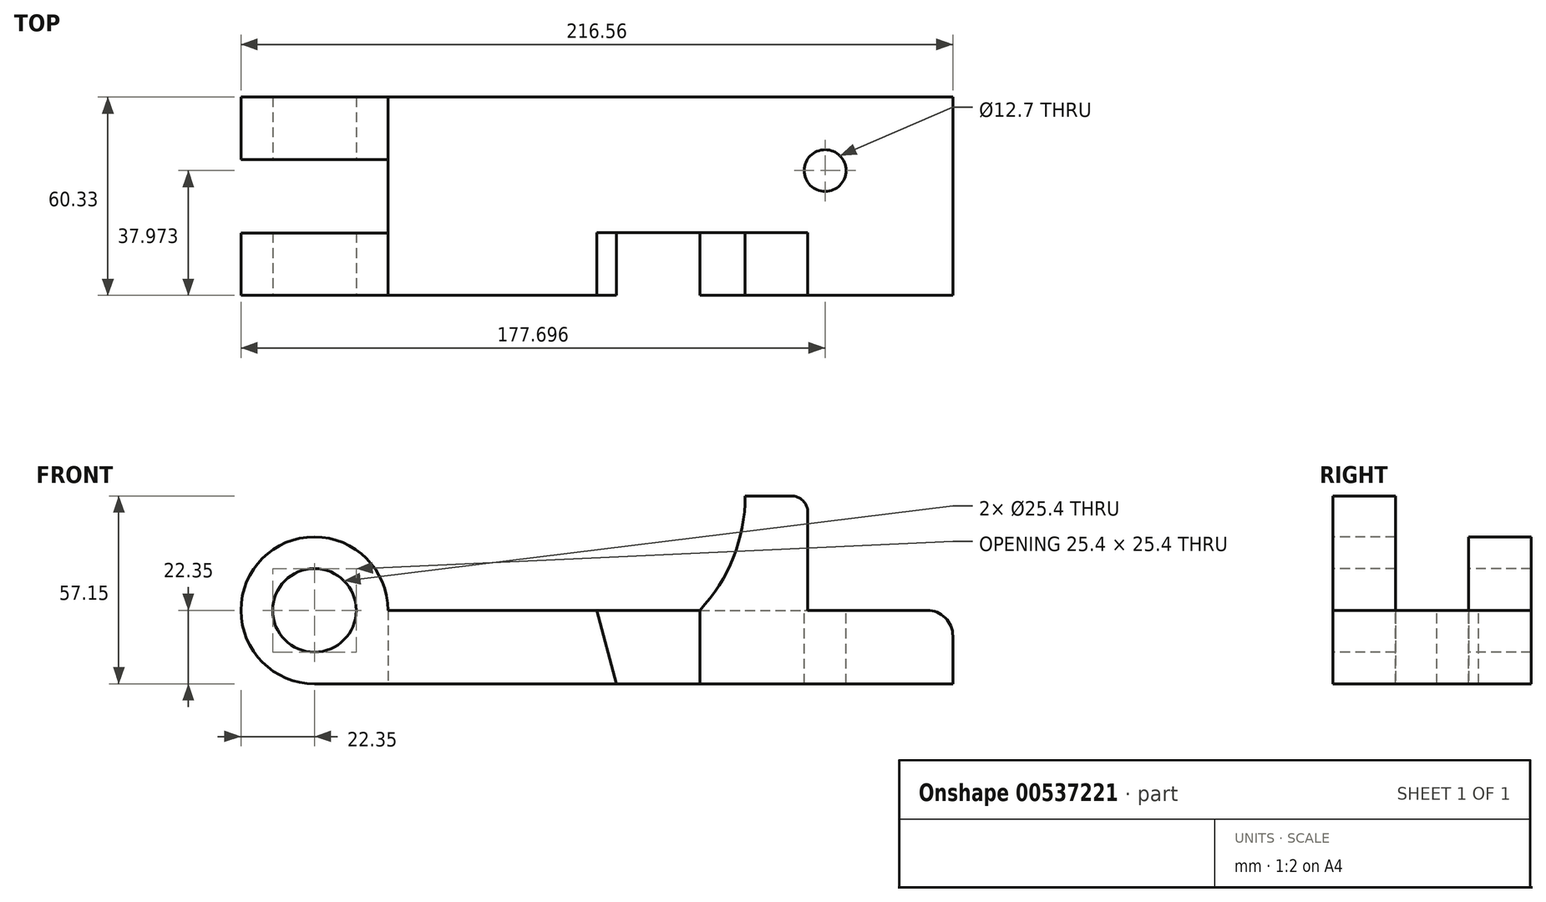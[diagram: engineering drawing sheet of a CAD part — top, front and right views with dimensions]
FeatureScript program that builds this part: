
annotation { "Feature Type Name" : "Feature", "Feature Type Description" : "" }
export const myFeature = defineFeature(function(context is Context, id is Id, definition is map)
    precondition{}
    {
        {
            var Q0;
            Q0=qCreatedBy(makeId("Front.planeOp"),FACE);
            var sketch = newSketch(context, id + "F0", { "sketchPlane" : qUnion([Q0])});
            skCircle(sketch, "E0", {"center": v(0, 0) * mm, "radius": 22.35 * mm});
            skCircle(sketch, "E1", {"center": v(0, 0) * mm, "radius": 12.7 * mm});
            skLineSegment(sketch, "E2", {"start": v(0, -22.35) * mm, "end": v(91.85, -22.35) * mm});
            skLineSegment(sketch, "E3", {"start": v(91.85, -22.35) * mm, "end": v(117.25, -22.35) * mm});
            skLineSegment(sketch, "E4", {"start": v(117.25, -22.35) * mm, "end": v(194.2, -22.35) * mm});
            skLineSegment(sketch, "E5", {"start": v(0, 62.8) * mm, "end": v(0, -59.04) * mm, "construction": true});
            skLineSegment(sketch, "E6", {"start": v(22.35, 0) * mm, "end": v(85.85, 0) * mm});
            skLineSegment(sketch, "E7", {"start": v(85.85, 0) * mm, "end": v(91.85, -22.35) * mm});
            skLineSegment(sketch, "E8", {"start": v(117.25, 0) * mm, "end": v(117.25, -22.35) * mm});
            skLineSegment(sketch, "E9", {"start": v(85.85, 0) * mm, "end": v(117.25, 0) * mm});
            skPoint(sketch, "E10", {"position": v(-22.35, 0) * mm});
            skLineSegment(sketch, "E11", {"start": v(194.2, -22.35) * mm, "end": v(194.2, -7.87) * mm});
            skPoint(sketch, "E11.endSnap0", {"position": v(54.1, 0) * mm});
            skLineSegment(sketch, "E12", {"start": v(186.33, 0) * mm, "end": v(150.09, 0) * mm});
            skLineSegment(sketch, "E13", {"start": v(150.09, 0) * mm, "end": v(150.09, 29.72) * mm});
            skLineSegment(sketch, "E14", {"start": v(145, 34.8) * mm, "end": v(131.04, 34.8) * mm});
            skArc(sketch, "E15", {"start": v(117.25, 0) * mm, "mid": v(127.46, 16.08) * mm, "end": v(131.04, 34.8) * mm});
            skPoint(sketch, "E16.visualSharp", {"position": v(150.09, 34.8) * mm});
            skArc(sketch, "E16.filletArc", {"start": v(150.09, 29.72) * mm, "mid": v(148.6, 33.31) * mm, "end": v(145, 34.8) * mm});
            skPoint(sketch, "E17.visualSharp", {"position": v(194.2, 0) * mm});
            skArc(sketch, "E17.filletArc", {"start": v(194.2, -7.87) * mm, "mid": v(191.9, -2.3) * mm, "end": v(186.33, 0) * mm});
            skLineSegment(sketch, "E18", {"start": v(117.25, 0) * mm, "end": v(150.09, 0) * mm});
            skSolve(sketch);
        }
        {
            var Q0;
            Q0=makeQuery(id+"F0.imprint","IMPRINT",FACE,{"disambiguationData":[TD([[makeQuery(id+"F0.imprint","IMPRINT",EDGE,{"derivedFrom":sQuery(id+"F0.wireOp",EDGE,"E1")}),-1.0]])]});
            extrude(context, id + "F1", {"entities" : qUnion([Q0]), "oppositeDirection" : true, "depth" : 60.32 * mm, "offsetDistance" : 25.4 * mm});
        }
        {
            var Q0;
            Q0=makeQuery(id+"F0.imprint","IMPRINT",FACE,{"disambiguationData":[TD([[makeQuery(id+"F0.imprint","IMPRINT",EDGE,{"derivedFrom":sQuery(id+"F0.wireOp",EDGE,"E4")}),1.0]])]});
            var Q1;
            {var subQ0=sQuery(id+"F0.wireOp",EDGE,"E2");Q1=makeQuery(id+"F0.imprint","IMPRINT",FACE,{"disambiguationData":[TD([[makeQuery(id+"F0.imprint","IMPRINT",EDGE,{"derivedFrom":subQ0}),1.0]])]});}
            extrude(context, id + "F2", {"entities" : qUnion([Q0, Q1]), "operationType" : NewBodyOperationType.ADD, "oppositeDirection" : true, "depth" : 60.32 * mm, "offsetDistance" : 25.4 * mm});
        }
        {
            var Q0;
            Q0=makeQuery(id+"F0.imprint","IMPRINT",FACE,{"disambiguationData":[TD([[makeQuery(id+"F0.imprint","IMPRINT",EDGE,{"derivedFrom":sQuery(id+"F0.wireOp",EDGE,"E3")}),1.0]])]});
            var Q1;
            Q1=makeQuery(id+"F2.opExtrude","CAP_VERTEX",VERTEX,{"disambiguationData":[OSD([sQuery(id+"F0.wireOp",EDGE,"E8"),sQuery(id+"F0.wireOp",EDGE,"E9"),sQuery(id+"F0.wireOp",EDGE,"E15")])],"isStart":false});
            extrude(context, id + "F3", {"entities" : qUnion([Q0]), "operationType" : NewBodyOperationType.ADD, "endBound" : BoundingType.UP_TO_VERTEX, "oppositeDirection" : true, "depth" : 97.03 * mm, "endBoundEntityVertex" : qUnion([Q1]), "offsetDistance" : 25.4 * mm});
        }
        {
            var Q0;
            Q0=makeQuery(id+"F0.imprint","IMPRINT",FACE,{"disambiguationData":[TD([[makeQuery(id+"F0.imprint","IMPRINT",EDGE,{"derivedFrom":sQuery(id+"F0.wireOp",EDGE,"E3")}),1.0]])]});
            extrude(context, id + "F4", {"entities" : qUnion([Q0]), "operationType" : NewBodyOperationType.REMOVE, "oppositeDirection" : true, "depth" : 19.05 * mm, "offsetDistance" : 25.4 * mm});
        }
        {
            var Q0;
            Q0=makeQuery(id+"F0.imprint","IMPRINT",FACE,{"disambiguationData":[TD([[makeQuery(id+"F0.imprint","IMPRINT",EDGE,{"derivedFrom":sQuery(id+"F0.wireOp",EDGE,"E13")}),1.0]])]});
            extrude(context, id + "F5", {"entities" : qUnion([Q0]), "operationType" : NewBodyOperationType.ADD, "oppositeDirection" : true, "depth" : 19.05 * mm, "offsetDistance" : 25.4 * mm});
        }
        {
            var Q0;
            Q0=qCreatedBy(makeId("Top.planeOp"),FACE);
            var sketch = newSketch(context, id + "F6", { "sketchPlane" : qUnion([Q0])});
            skLineSegment(sketch, "E19", {"start": v(22.35, 0) * mm, "end": v(22.35, 60.33) * mm});
            skLineSegment(sketch, "E20", {"start": v(-22.35, 0) * mm, "end": v(-22.35, 19) * mm, "construction": true});
            skLineSegment(sketch, "E21", {"start": v(-22.35, 60.33) * mm, "end": v(-22.35, 41.33) * mm, "construction": true});
            skLineSegment(sketch, "E22", {"start": v(-22.35, 41.33) * mm, "end": v(22.35, 41.33) * mm});
            skLineSegment(sketch, "E23", {"start": v(-22.35, 41.33) * mm, "end": v(-22.35, 19) * mm});
            skLineSegment(sketch, "E24", {"start": v(22.35, 19) * mm, "end": v(22.35, 41.33) * mm});
            skLineSegment(sketch, "E25", {"start": v(-22.35, 19) * mm, "end": v(22.35, 19) * mm});
            skSolve(sketch);
        }
        {
            var Q0;
            Q0 = qSketchRegion(id + "F6", true);
            extrude(context, id + "F7", {"entities" : qUnion([Q0]), "operationType" : NewBodyOperationType.REMOVE, "depth" : 73.66 * mm, "offsetDistance" : 25.4 * mm, "symmetric" : true});
        }
        {
            var Q0;
            Q0=makeQuery(id+"F3.boolean.opBoolean","MERGE",FACE,{"derivedFrom":[makeQuery(id+"F2.opExtrude","SWEPT_FACE",FACE,{"disambiguationData":[OSD([sQuery(id+"F0.wireOp",EDGE,"E6")])]}),makeQuery(id+"F2.opExtrude","SWEPT_FACE",FACE,{"disambiguationData":[OSD([sQuery(id+"F0.wireOp",EDGE,"E12"),sQuery(id+"F0.wireOp",EDGE,"E18")])]}),makeQuery(id+"F3.opExtrude","SWEPT_FACE",FACE,{"disambiguationData":[OSD([sQuery(id+"F0.wireOp",EDGE,"E9")])]})]});
            var sketch = newSketch(context, id + "F8", { "sketchPlane" : qUnion([Q0])});
            skLineSegment(sketch, "E26.0", {"start": v(194.2, 60.33) * mm, "end": v(186.33, 60.33) * mm});
            skLineSegment(sketch, "E27", {"start": v(194.2, 60.33) * mm, "end": v(155.35, 60.33) * mm, "construction": true});
            skLineSegment(sketch, "E28", {"start": v(155.35, 60.33) * mm, "end": v(155.35, 37.97) * mm, "construction": true});
            skCircle(sketch, "E29", {"center": v(155.35, 37.97) * mm, "radius": 6.35 * mm});
            skSolve(sketch);
        }
        {
            var Q0;
            Q0 = qSketchRegion(id + "F8", true);
            extrude(context, id + "F9", {"entities" : qUnion([Q0]), "operationType" : NewBodyOperationType.REMOVE, "oppositeDirection" : true, "depth" : 25.4 * mm, "offsetDistance" : 25.4 * mm});
        }
    });
